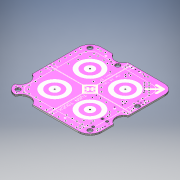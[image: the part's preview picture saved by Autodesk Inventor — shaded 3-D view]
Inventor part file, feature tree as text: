
AUTODESK INVENTOR PART (.ipt)
format: ipt  version: 2016 (Build 200138000, 138)  size: 3,613,184 bytes
history: native  units: in
note: dims shown in document units (in); Inventor stores cm internally (conversion verified against a paired STEP export)
features: other x5, sketch x2, extrude x1, move_body x1
ambient origin geometry x8: Origin, YZ Plane, XZ Plane, XY Plane, X Axis, Y Axis, Z Axis, Center Point
bodies: Solid1 (feature_tree)
feature tree (9):
  extrude  "Extrusion1"  Depth=0.026in TaperAngle=0.0deg
  move_body  "Move Body1"
  other  "Decal1"
  other  "Decal2"
  other  "PCB"
  sketch  "Sketch3"  dims[d0=1.453in d1=0.026in d2=0.0in]
  other  "Image1"
  sketch  "Sketch4"  dims[d3=270.0deg d4=270.0deg]
  other  "Image2"
